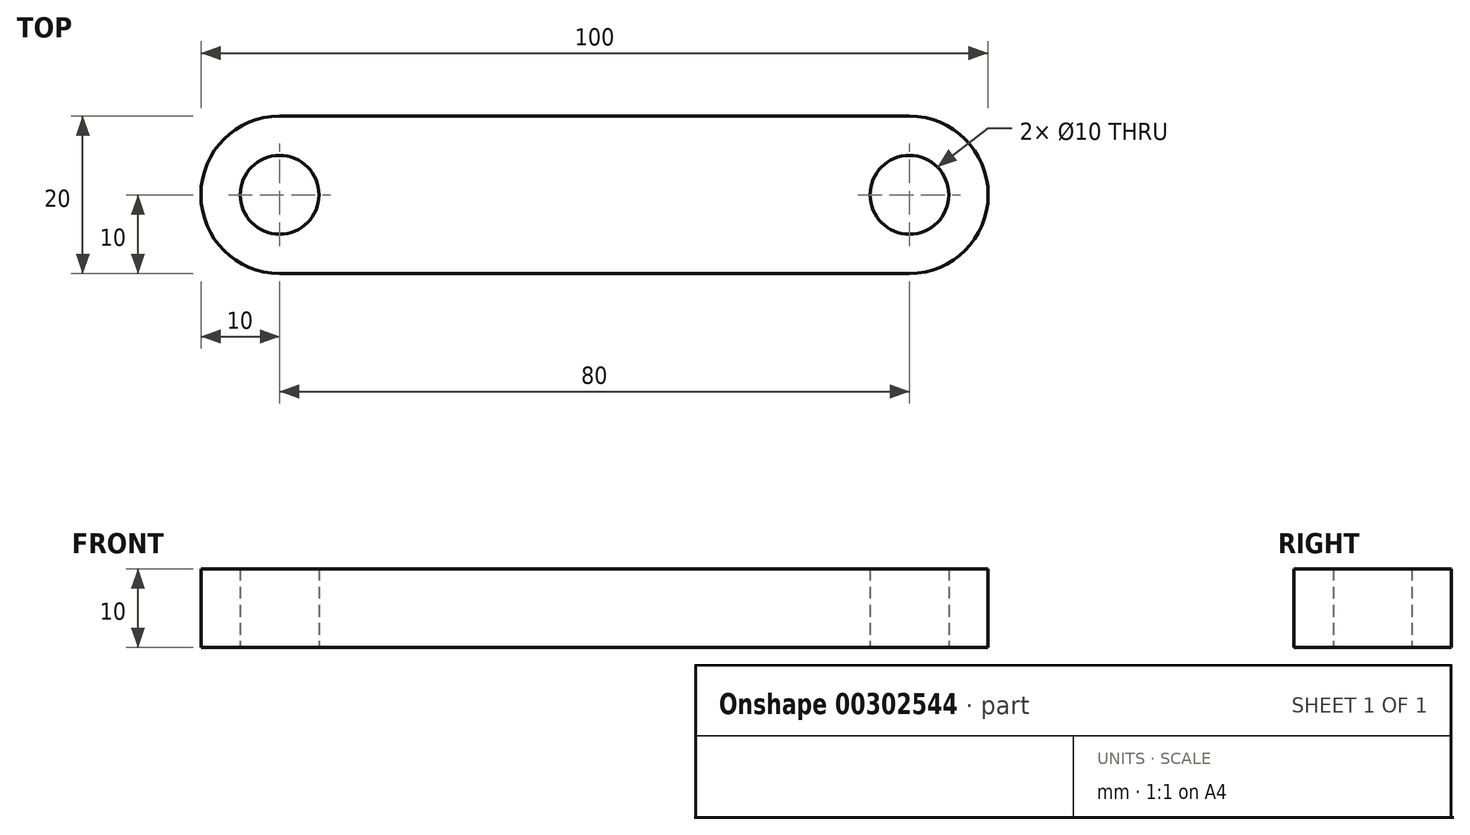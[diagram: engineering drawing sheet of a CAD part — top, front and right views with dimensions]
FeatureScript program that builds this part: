
annotation { "Feature Type Name" : "Feature", "Feature Type Description" : "" }
export const myFeature = defineFeature(function(context is Context, id is Id, definition is map)
    precondition{}
    {
        {
            var Q0;
            Q0=qCreatedBy(makeId("Top.planeOp"),FACE);
            var sketch = newSketch(context, id + "F0", { "sketchPlane" : qUnion([Q0])});
            skLineSegment(sketch, "E0", {"start": v(0, 0) * mm, "end": v(0, 20) * mm});
            skLineSegment(sketch, "E1", {"start": v(0, 20) * mm, "end": v(80, 20) * mm});
            skLineSegment(sketch, "E2", {"start": v(80, 20) * mm, "end": v(80, 0) * mm});
            skLineSegment(sketch, "E3", {"start": v(80, 0) * mm, "end": v(0, 0) * mm});
            skArc(sketch, "E4", {"start": v(80, 0) * mm, "mid": v(90, 10) * mm, "end": v(80, 20) * mm});
            skArc(sketch, "E5", {"start": v(0, 20) * mm, "mid": v(-10, 10) * mm, "end": v(0, 0) * mm});
            skCircle(sketch, "E6", {"center": v(0, 10) * mm, "radius": 5 * mm});
            skCircle(sketch, "E7", {"center": v(80, 10) * mm, "radius": 5 * mm});
            skSolve(sketch);
        }
        {
            var Q0;
            {var subQ2=sQuery(id+"F0.wireOp",EDGE,"E1");Q0=makeQuery(id+"F0.imprint","IMPRINT",FACE,{"disambiguationData":[TD([[makeQuery(id+"F0.imprint","IMPRINT",EDGE,{"derivedFrom":subQ2}),-1.0]])]});}
            var Q1;
            Q1 = qSketchRegion(id + "F0", true);
            extrude(context, id + "F1", {"entities" : qUnion([Q0, Q1]), "depth" : 10 * mm});
        }
    });
